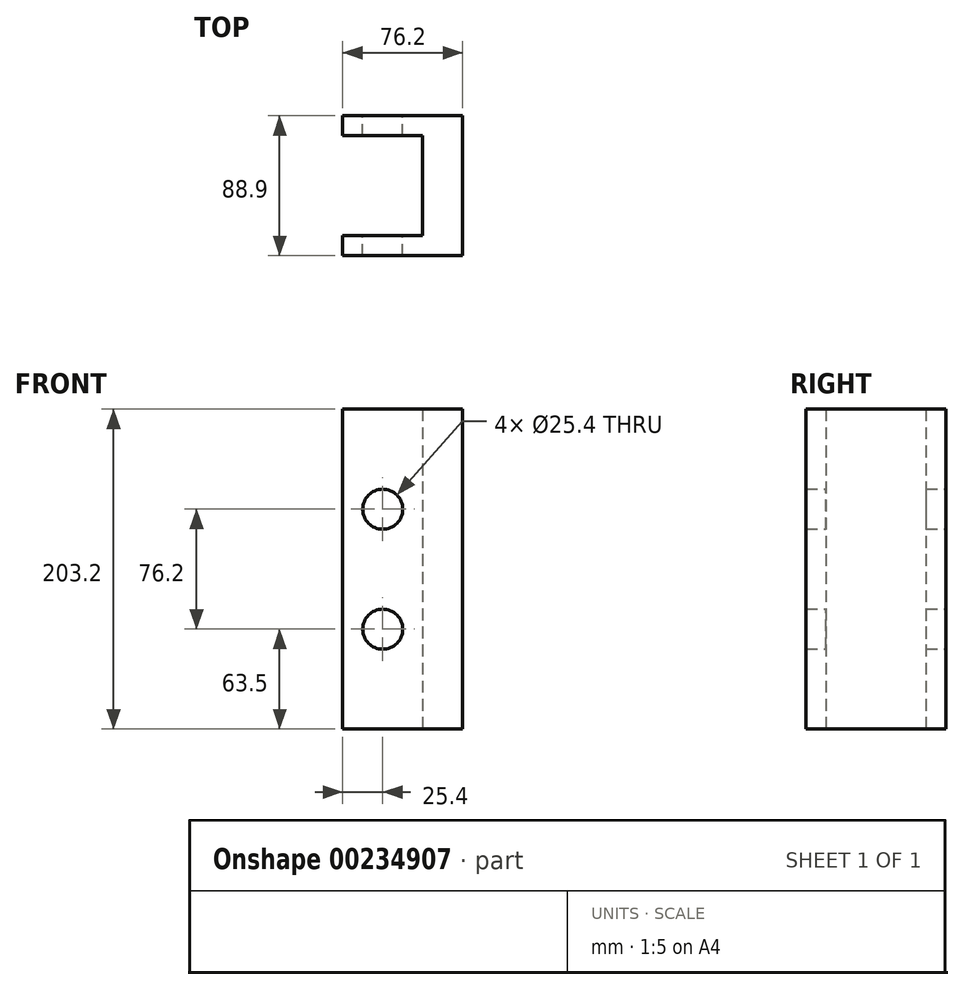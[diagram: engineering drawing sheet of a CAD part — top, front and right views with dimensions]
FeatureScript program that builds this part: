
annotation { "Feature Type Name" : "Feature", "Feature Type Description" : "" }
export const myFeature = defineFeature(function(context is Context, id is Id, definition is map)
    precondition{}
    {
        {
            var Q0;
            Q0=qCreatedBy(makeId("Top.planeOp"),FACE);
            var sketch = newSketch(context, id + "F0", { "sketchPlane" : qUnion([Q0])});
            skLineSegment(sketch, "E0", {"start": v(-50.8, 44.45) * mm, "end": v(-50.8, 31.75) * mm});
            skLineSegment(sketch, "E1", {"start": v(-50.8, 31.75) * mm, "end": v(0, 31.75) * mm});
            skLineSegment(sketch, "E2", {"start": v(0, 31.75) * mm, "end": v(0, -31.75) * mm});
            skLineSegment(sketch, "E3", {"start": v(0, -31.75) * mm, "end": v(-50.8, -31.75) * mm});
            skLineSegment(sketch, "E4", {"start": v(-50.8, -31.75) * mm, "end": v(-50.8, -44.45) * mm});
            skLineSegment(sketch, "E5", {"start": v(-50.8, -44.45) * mm, "end": v(25.4, -44.45) * mm});
            skLineSegment(sketch, "E6", {"start": v(25.4, -44.45) * mm, "end": v(25.4, 44.45) * mm});
            skLineSegment(sketch, "E7", {"start": v(25.4, 44.45) * mm, "end": v(-50.8, 44.45) * mm});
            skSolve(sketch);
        }
        {
            var Q0;
            Q0=makeQuery(id+"F0.imprint","IMPRINT",FACE,{"disambiguationData":[TD([[makeQuery(id+"F0.imprint","IMPRINT",EDGE,{"derivedFrom":sQuery(id+"F0.wireOp",EDGE,"E0")}),1.0]])]});
            extrude(context, id + "F1", {"entities" : qUnion([Q0]), "depth" : 203.2 * mm});
        }
        {
            var Q0;
            Q0=makeQuery(id+"F1.opExtrude","SWEPT_FACE",FACE,{"disambiguationData":[OSD([sQuery(id+"F0.wireOp",EDGE,"E7")])]});
            var sketch = newSketch(context, id + "F2", { "sketchPlane" : qUnion([Q0])});
            skCircle(sketch, "E8", {"center": v(25.4, 63.5) * mm, "radius": 12.7 * mm});
            skCircle(sketch, "E9", {"center": v(25.4, 139.7) * mm, "radius": 12.7 * mm});
            skSolve(sketch);
        }
        {
            var Q0;
            Q0=makeQuery(id+"F2.imprint","IMPRINT",FACE,{"disambiguationData":[TD([[makeQuery(id+"F2.imprint","IMPRINT",EDGE,{"derivedFrom":sQuery(id+"F2.wireOp",EDGE,"E9")}),1.0]])]});
            var Q1;
            Q1=makeQuery(id+"F2.imprint","IMPRINT",FACE,{"disambiguationData":[TD([[makeQuery(id+"F2.imprint","IMPRINT",EDGE,{"derivedFrom":sQuery(id+"F2.wireOp",EDGE,"E8")}),1.0]])]});
            extrude(context, id + "F3", {"entities" : qUnion([Q0, Q1]), "operationType" : NewBodyOperationType.REMOVE, "endBound" : BoundingType.THROUGH_ALL, "oppositeDirection" : true, "depth" : 25.4 * mm});
        }
    });
